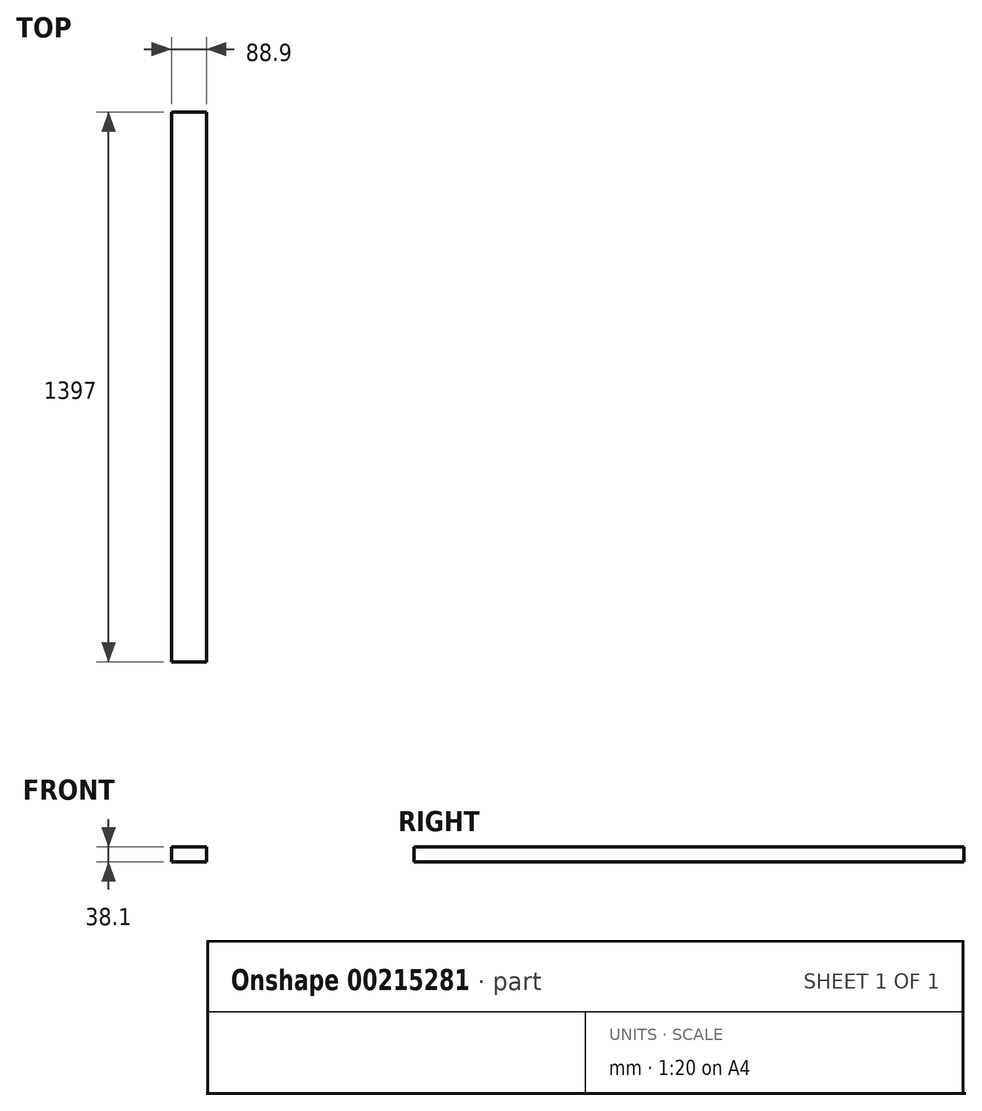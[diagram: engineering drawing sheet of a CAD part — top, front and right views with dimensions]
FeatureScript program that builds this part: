
annotation { "Feature Type Name" : "Feature", "Feature Type Description" : "" }
export const myFeature = defineFeature(function(context is Context, id is Id, definition is map)
    precondition{}
    {
        {
            var Q0;
            Q0=qCreatedBy(makeId("Top.planeOp"),FACE);
            var sketch = newSketch(context, id + "F0", { "sketchPlane" : qUnion([Q0])});
            skLineSegment(sketch, "E0.bottom", {"start": v(-44.45, 698.5) * mm, "end": v(44.45, 698.5) * mm});
            skLineSegment(sketch, "E0.top", {"start": v(-44.45, -698.5) * mm, "end": v(44.45, -698.5) * mm});
            skLineSegment(sketch, "E0.left", {"start": v(-44.45, 698.5) * mm, "end": v(-44.45, -698.5) * mm});
            skLineSegment(sketch, "E0.right", {"start": v(44.45, 698.5) * mm, "end": v(44.45, -698.5) * mm});
            skSolve(sketch);
        }
        {
            var Q0;
            Q0=makeQuery(id+"F0.imprint","IMPRINT",FACE,{"disambiguationData":[TD([[makeQuery(id+"F0.imprint","IMPRINT",EDGE,{"derivedFrom":sQuery(id+"F0.wireOp",EDGE,"E0.bottom")}),-1.0]])]});
            extrude(context, id + "F1", {"entities" : qUnion([Q0]), "depth" : 38.1 * mm});
        }
    });
